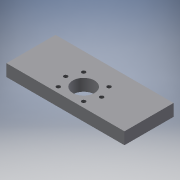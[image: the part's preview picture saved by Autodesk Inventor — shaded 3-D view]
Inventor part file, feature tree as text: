
AUTODESK INVENTOR PART (.ipt)
format: ipt  version: 2018 (Build 220112000, 112)  size: 133,120 bytes
history: native  units: mm
features: sketch x3, hole x2, other x1, extrude x1
ambient origin geometry x8: Origin, YZ Plane, XZ Plane, XY Plane, X Axis, Y Axis, Z Axis, Center Point
bodies: Body1 (feature_tree)
feature tree (7):
  other  "Sólido1"
  extrude  "Extrusão1"  Depth=52.0mm
  hole  "Furo2"  [1 undecoded]
  hole  "Furo3"  [1 undecoded]
  sketch  "Esboço1"  dims[d0=52.0mm d1=23.0mm]
  sketch  "Esboço3"  dims[d2=125.0mm d3=12.7mm d4=0.0mm]
  sketch  "Esboço5"  dims[d18=4.134mm d19=10.0mm d20=4.0mm d21=2.0mm d22=90.0deg d23=14.2mm d24=20.594885mm d25=5.5mm d26=10.0mm d27=8.0mm d28=6.0mm d29=90.0deg d30=14.2mm d31=20.594885mm]
note: 2 required parameter values undecoded (feature->parameter linkage not recoverable at this tier; creation-order binding heuristic only, values carry confidence <= 0.55)
